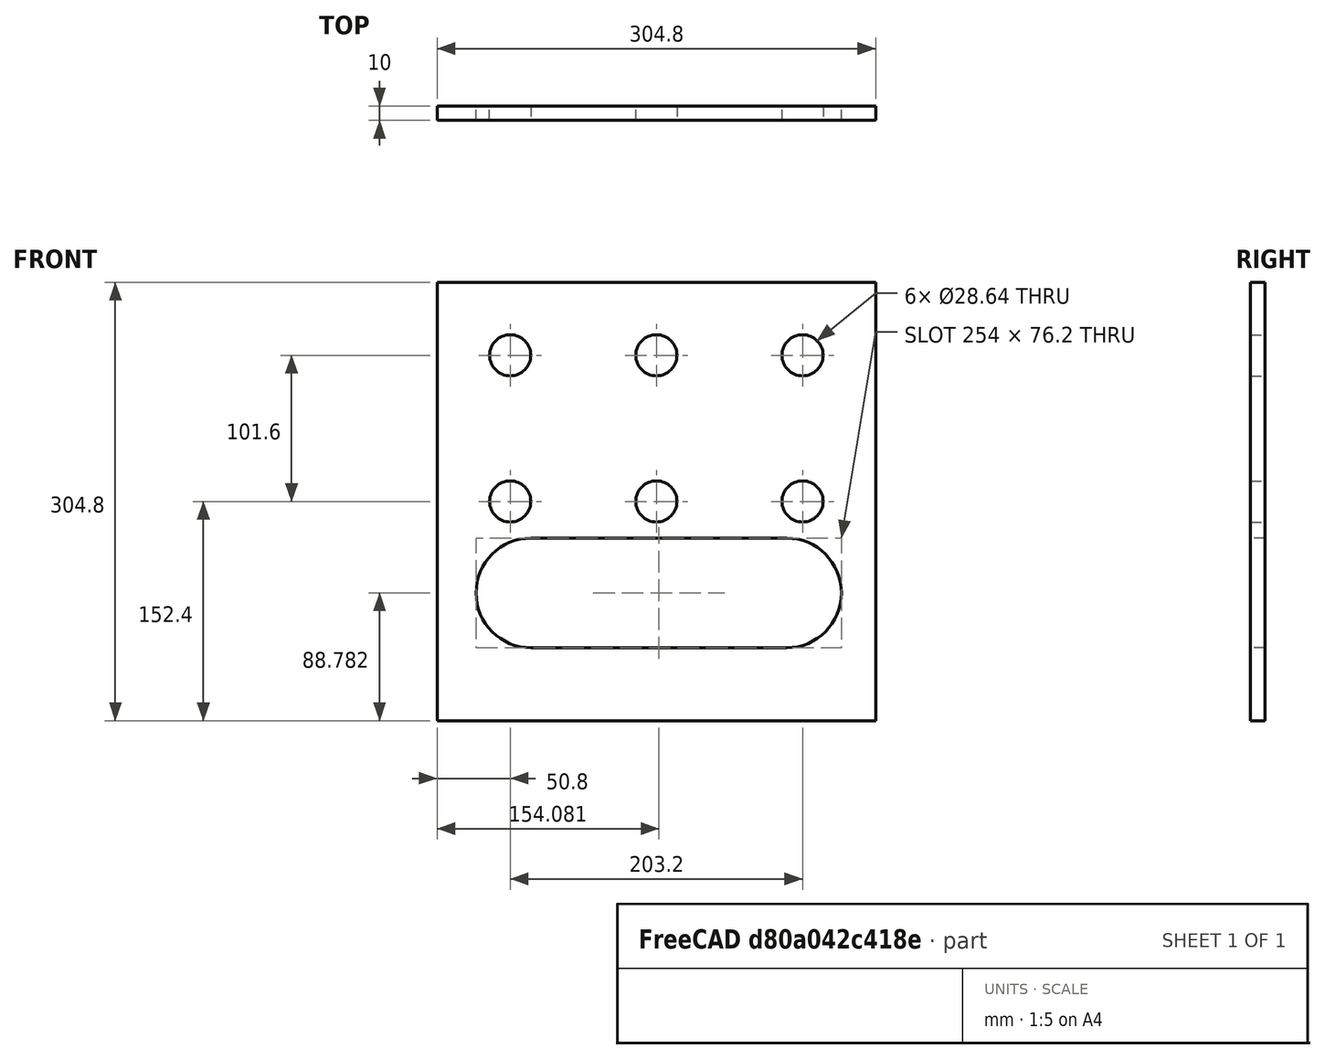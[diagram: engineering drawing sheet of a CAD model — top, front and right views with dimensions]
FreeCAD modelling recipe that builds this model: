
FCSTD DOCUMENT  (FreeCAD 0.16R6668 (Git))
Label: idleradjuster
License: All rights reserved
LicenseURL: http://en.wikipedia.org/wiki/All_rights_reserved
objects: Sketcher::SketchObject×1, PartDesign::Pad×1
note: 3 computed .brp shape members not serialized (recipe doc carries the construction recipe); baked Part::Feature solids carry a one-line shape summary decoded from their .brp

FEATURE [Sketcher::SketchObject] Sketch
  Placement = pos=(0,0,0) rot=(1,0,0;1.5708rad)
  sketch-geometry (14):
    g0: LineSegment StartX=-152.4 StartY=152.4 StartZ=0 EndX=152.4 EndY=152.4 EndZ=0
    g1: LineSegment StartX=152.4 StartY=152.4 StartZ=0 EndX=152.4 EndY=-152.4 EndZ=0
    g2: LineSegment StartX=152.4 StartY=-152.4 StartZ=0 EndX=-152.4 EndY=-152.4 EndZ=0
    g3: LineSegment StartX=-152.4 StartY=-152.4 StartZ=0 EndX=-152.4 EndY=152.4 EndZ=0
    g4: Circle CenterX=101.6 CenterY=101.6 CenterZ=0 NormalX=0 NormalY=0 NormalZ=1 Radius=14.3183
    g5: Circle CenterX=-101.6 CenterY=0 CenterZ=0 NormalX=0 NormalY=0 NormalZ=1 Radius=14.3183
    g6: Circle CenterX=101.6 CenterY=0 CenterZ=0 NormalX=0 NormalY=0 NormalZ=1 Radius=14.3183
    g7: Circle CenterX=0 CenterY=101.6 CenterZ=0 NormalX=0 NormalY=0 NormalZ=1 Radius=14.3183
    g8: Circle CenterX=0 CenterY=0 CenterZ=0 NormalX=0 NormalY=0 NormalZ=1 Radius=14.3183
    g9: Circle CenterX=-101.6 CenterY=101.6 CenterZ=0 NormalX=0 NormalY=0 NormalZ=1 Radius=14.3183
    g10: ArcOfCircle CenterX=-87.2191 CenterY=-63.618 CenterZ=0 NormalX=0 NormalY=0 NormalZ=1 Radius=38.1 StartAngle=1.5708 EndAngle=4.71239
    g11: ArcOfCircle CenterX=90.5809 CenterY=-63.618 CenterZ=0 NormalX=0 NormalY=0 NormalZ=1 Radius=38.1 StartAngle=4.71239 EndAngle=7.85398
    g12: LineSegment StartX=-87.2191 StartY=-101.718 StartZ=0 EndX=90.5809 EndY=-101.718 EndZ=0
    g13: LineSegment StartX=-87.2191 StartY=-25.518 StartZ=0 EndX=90.5809 EndY=-25.518 EndZ=0
  constraints (27):
    c: Coincident(g0,g1)
    c: Coincident(g1,g2)
    c: Coincident(g2,g3)
    c: Coincident(g3,g0)
    c: Horizontal(g0)
    c: Horizontal(g2)
    c: Vertical(g1)
    c: Vertical(g3)
    c: DistanceX(g2,g2) = 304.8
    c: DistanceY(g1,g1) = 304.8
    c: Equal(g4,g5)
    c: Equal(g1,g3)
    c: Equal(g0,g2)
    c: Equal(g4,g6)
    c: DistanceX(g6,g1) = 50.8
    c: DistanceY(g1,g6) = 152.4
    c: DistanceY(g2,g5) = 152.4
    c: Equal(g4,g7)
    c: Equal(g7,g9)
    c: Equal(g9,g8)
    c: Tangent(g10,g13) = 1.5708
    c: Tangent(g10,g12) = -1.5708
    c: Tangent(g12,g11) = -1.5708
    c: Tangent(g13,g11) = 1.5708
    c: Horizontal(g12)
    c: Equal(g10,g11)
    c: DistanceY(g10,g10) = 76.2
FEATURE [PartDesign::Pad] Pad
  Length = 10
  Length2 = 100
  Placement = pos=(0,0,0) rot=(1,0,0;1.5708rad)
  Sketch = -> Sketch
  Type = 0
